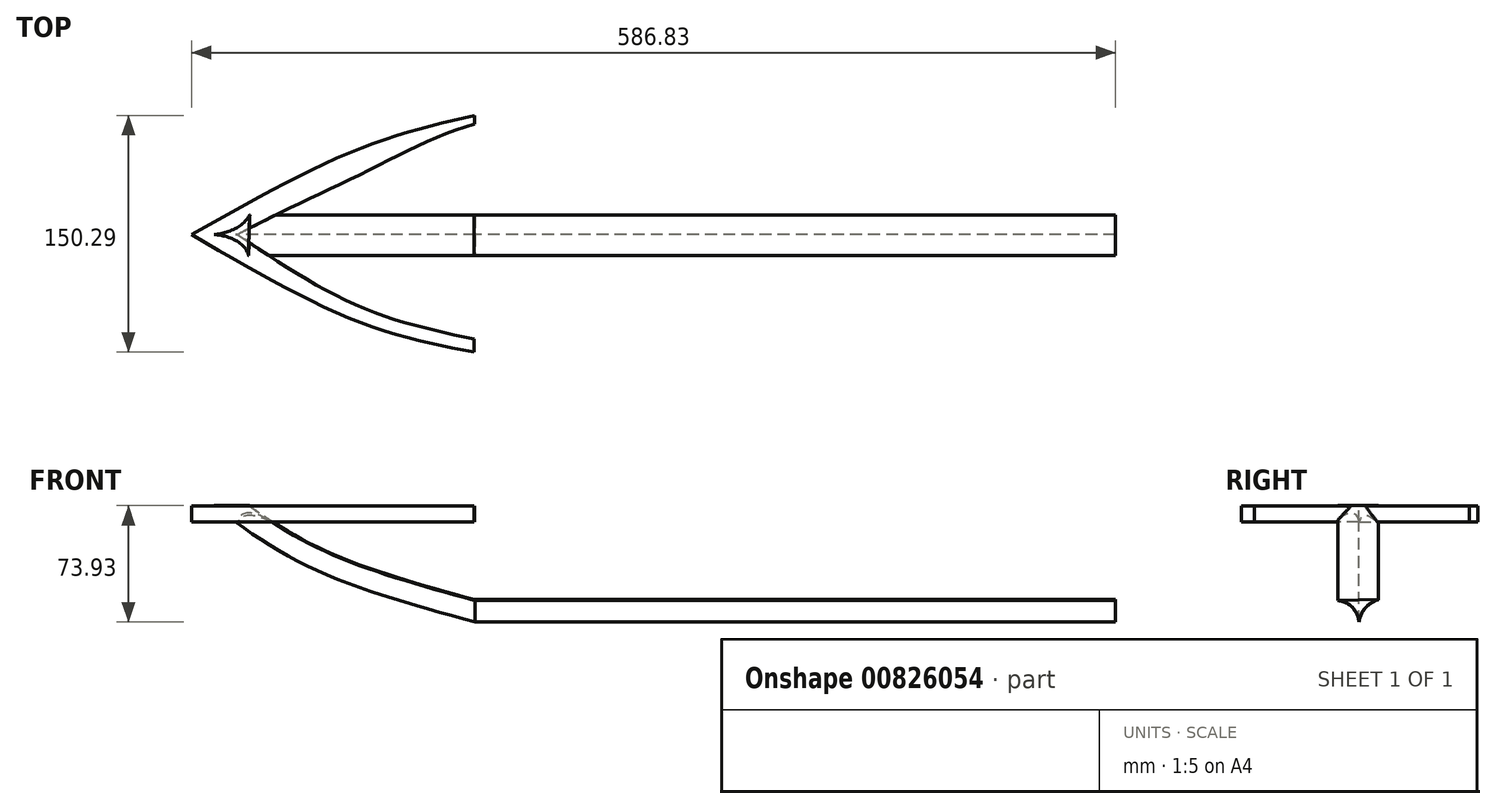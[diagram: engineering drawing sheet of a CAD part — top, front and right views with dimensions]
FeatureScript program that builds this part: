
annotation { "Feature Type Name" : "Feature", "Feature Type Description" : "" }
export const myFeature = defineFeature(function(context is Context, id is Id, definition is map)
    precondition{}
    {
        {
            var Q0;
            Q0=qCreatedBy(makeId("Right.planeOp"),FACE);
            var sketch = newSketch(context, id + "F0", { "sketchPlane" : qUnion([Q0])});
            skArc(sketch, "E0", {"start": v(12.35, -22.84) * mm, "mid": v(49.48, 1.71) * mm, "end": v(76.48, 37.1) * mm});
            skArc(sketch, "E1", {"start": v(-76.36, 37.1) * mm, "mid": v(-50.13, 1.38) * mm, "end": v(-13.34, -23.31) * mm});
            skArc(sketch, "E2", {"start": v(12.35, -22.84) * mm, "mid": v(4.12, -28.11) * mm, "end": v(0, -36.97) * mm});
            skArc(sketch, "E3", {"start": v(0, -36.97) * mm, "mid": v(-4.21, -27.74) * mm, "end": v(-13.34, -23.31) * mm});
            skLineSegment(sketch, "E4", {"start": v(0, -36.97) * mm, "end": v(0, -50.64) * mm});
            skLineSegment(sketch, "E5", {"start": v(12.35, -22.84) * mm, "end": v(-13.34, -23.31) * mm});
            skArc(sketch, "E6", {"start": v(0, -17.04) * mm, "mid": v(40.45, 2.58) * mm, "end": v(69.45, 36.93) * mm});
            skArc(sketch, "E7", {"start": v(-70.42, 37.1) * mm, "mid": v(-40.79, 2.77) * mm, "end": v(0, -17.04) * mm});
            skLineSegment(sketch, "E8", {"start": v(-70.42, 37.1) * mm, "end": v(-76.36, 37.1) * mm});
            skLineSegment(sketch, "E9", {"start": v(76.48, 37.1) * mm, "end": v(69.45, 36.93) * mm});
            skSolve(sketch);
        }
        {
            var Q0;
            Q0 = qSketchRegion(id + "F0", true);
            var Q1;
            Q1=sQuery(id+"F0.wireOp",EDGE,"E1");
            var Q2;
            Q2=sQuery(id+"F0.wireOp",EDGE,"E3");
            var Q3;
            Q3=sQuery(id+"F0.wireOp",EDGE,"E2");
            var Q4;
            Q4=sQuery(id+"F0.wireOp",EDGE,"E0");
            extrude(context, id + "F1", {"entities" : qUnion([Q0]), "bodyType" : ToolBodyType.SURFACE, "surfaceEntities" : qUnion([Q1, Q2, Q3, Q4]), "endBound" : BoundingType.SYMMETRIC, "depth" : 407.62 * mm, "offsetDistance" : 25.4 * mm});
        }
        {
            var Q0;
            Q0=makeQuery(id+"F0.imprint","IMPRINT",FACE,{"disambiguationData":[TD([[makeQuery(id+"F0.imprint","IMPRINT",EDGE,{"derivedFrom":sQuery(id+"F0.wireOp",EDGE,"E2")}),-1.0]])]});
            extrude(context, id + "F2", {"entities" : qUnion([Q0]), "endBound" : BoundingType.SYMMETRIC, "depth" : 407.33 * mm, "offsetDistance" : 25.4 * mm});
        }
        {
            var Q0;
            Q0=qCreatedBy(makeId("Front.planeOp"),FACE);
            var sketch = newSketch(context, id + "F3", { "sketchPlane" : qUnion([Q0])});
            skFitSpline(sketch, "E10", {"points": [v(-202.96, -36.94) * mm, v(-312.31, 0) * mm, v(-384.6, 49.56) * mm], "startDerivative": vector(-217.83, 59.17) * mm, "endDerivative": vector(-143.76, 115.11) * mm});
            skSolve(sketch);
        }
        {
            var Q0;
            Q0=makeQuery(id+"F2.opExtrude","CAP_FACE",FACE,{"disambiguationData":[OSD([sQuery(id+"F0.wireOp",EDGE,"E2"),sQuery(id+"F0.wireOp",EDGE,"E3"),sQuery(id+"F0.wireOp",EDGE,"E5")])],"isStart":true});
            var Q1;
            Q1=sQuery(id+"F3.wireOp",EDGE,"E10");
            sweep(context, id + "F4", {"operationType" : NewBodyOperationType.ADD, "profiles" : qUnion([Q0]), "path" : qUnion([Q1])});
        }
        {
            var Q0;
            Q0=qCreatedBy(makeId("Top.planeOp"),FACE);
            cPlane(context, id + "F5", {"entities" : qUnion([Q0]), "cplaneType" : CPlaneType.OFFSET, "offset" : 36.62 * mm, "width" : 152.4 * mm, "height" : 152.4 * mm});
        }
        {
            var Q0;
            Q0=qCreatedBy(id+"F5.planeOp",FACE);
            var sketch = newSketch(context, id + "F6", { "sketchPlane" : qUnion([Q0])});
            skFitSpline(sketch, "E11", {"points": [v(-383.17, 0) * mm, v(-277.14, 54.28) * mm, v(-203.38, 75.63) * mm], "startDerivative": vector(198.16, 111.53) * mm, "endDerivative": vector(158.98, 36.98) * mm});
            skFitSpline(sketch, "E12", {"points": [v(-383.17, 0) * mm, v(-277.14, -55.39) * mm, v(-203.82, -74.66) * mm], "startDerivative": vector(197.42, -115.07) * mm, "endDerivative": vector(159.87, -31.07) * mm});
            skFitSpline(sketch, "E13", {"points": [v(-354.08, 0) * mm, v(-274.8, 38.77) * mm, v(-203.38, 70.05) * mm], "startDerivative": vector(152.96, 81.79) * mm, "endDerivative": vector(147.37, 38.9) * mm});
            skFitSpline(sketch, "E14", {"points": [v(-354.08, 0) * mm, v(-277.14, -45.42) * mm, v(-203.82, -66.46) * mm], "startDerivative": vector(146.84, -98.71) * mm, "endDerivative": vector(153.78, -33.34) * mm});
            skLineSegment(sketch, "E15", {"start": v(-203.38, 75.63) * mm, "end": v(-203.38, 70.05) * mm});
            skLineSegment(sketch, "E16", {"start": v(-203.82, -66.46) * mm, "end": v(-203.82, -74.66) * mm});
            skSolve(sketch);
        }
        {
            var Q0;
            Q0 = qSketchRegion(id + "F6", true);
            extrude(context, id + "F7", {"entities" : qUnion([Q0]), "operationType" : NewBodyOperationType.ADD, "oppositeDirection" : true, "depth" : 10.27 * mm, "offsetDistance" : 25.4 * mm});
        }
        {
            var Q0;
            Q0=qCreatedBy(makeId("Right.planeOp"),FACE);
            var sketch = newSketch(context, id + "F8", { "sketchPlane" : qUnion([Q0])});
            skLineSegment(sketch, "E17.bottom", {"start": v(-14, 36.77) * mm, "end": v(13.83, 36.77) * mm});
            skLineSegment(sketch, "E17.top", {"start": v(-14, 68.38) * mm, "end": v(13.83, 68.38) * mm});
            skLineSegment(sketch, "E17.left", {"start": v(-14, 36.77) * mm, "end": v(-14, 68.38) * mm});
            skLineSegment(sketch, "E17.right", {"start": v(13.83, 36.77) * mm, "end": v(13.83, 68.38) * mm});
            skSolve(sketch);
        }
        {
            var Q0;
            Q0 = qSketchRegion(id + "F8", true);
            extrude(context, id + "F9", {"entities" : qUnion([Q0]), "operationType" : NewBodyOperationType.REMOVE, "oppositeDirection" : true, "depth" : 600.46 * mm, "offsetDistance" : 25.4 * mm});
        }
    });
